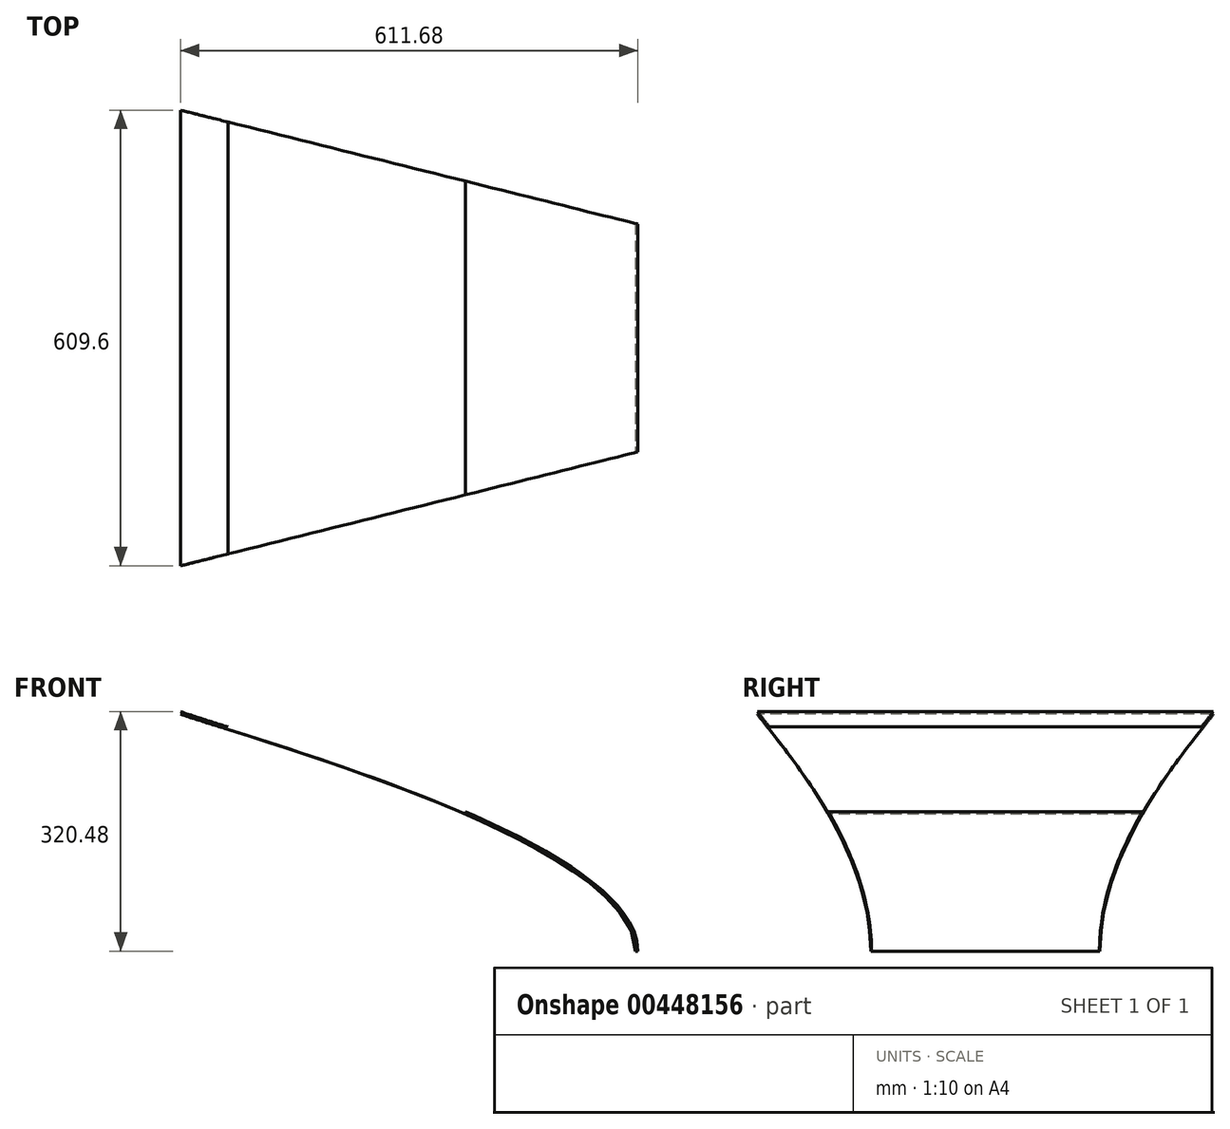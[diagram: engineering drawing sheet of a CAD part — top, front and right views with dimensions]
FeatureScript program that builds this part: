
annotation { "Feature Type Name" : "Feature", "Feature Type Description" : "" }
export const myFeature = defineFeature(function(context is Context, id is Id, definition is map)
    precondition{}
    {
        {
            var Q0;
            Q0=qCreatedBy(makeId("Front.planeOp"),FACE);
            var sketch = newSketch(context, id + "F0", { "sketchPlane" : qUnion([Q0])});
            skFitSpline(sketch, "E0", {"points": [v(-609.6, 317.5) * mm, v(0, 0) * mm], "startDerivative": vector(239.16, -88.23) * mm, "endDerivative": vector(0, -441.17) * mm});
            skSolve(sketch);
        }
        {
            var Q0;
            Q0=qCreatedBy(makeId("Top.planeOp"),FACE);
            var sketch = newSketch(context, id + "F1", { "sketchPlane" : qUnion([Q0])});
            skLineSegment(sketch, "E1.bottom", {"start": v(0, 304.8) * mm, "end": v(3.18, 304.8) * mm});
            skLineSegment(sketch, "E1.top", {"start": v(0, -304.8) * mm, "end": v(3.18, -304.8) * mm});
            skLineSegment(sketch, "E1.left", {"start": v(0, 304.8) * mm, "end": v(0, -304.8) * mm});
            skLineSegment(sketch, "E1.right", {"start": v(3.17, 304.8) * mm, "end": v(3.18, -304.8) * mm});
            skSolve(sketch);
        }
        {
            var Q0;
            Q0=makeQuery(id+"F1.imprint","IMPRINT",FACE,{"disambiguationData":[TD([[makeQuery(id+"F1.imprint","IMPRINT",EDGE,{"derivedFrom":sQuery(id+"F1.wireOp",EDGE,"E1.bottom")}),-1.0]])]});
            var Q1;
            Q1=sQuery(id+"F0.wireOp",EDGE,"E0");
            sweep(context, id + "F2", {"profiles" : qUnion([Q0]), "path" : qUnion([Q1])});
        }
        {
            var Q0;
            Q0=qCreatedBy(makeId("Top.planeOp"),FACE);
            var sketch = newSketch(context, id + "F3", { "sketchPlane" : qUnion([Q0])});
            skFitSpline(sketch, "E2.0.0", {"points": [v(3.17, 304.8) * mm, v(-200.72, 304.8) * mm, v(-404.6, 304.8) * mm, v(-608.5, 304.8) * mm]});
            skLineSegment(sketch, "E2.0.1", {"start": v(-608.5, -304.8) * mm, "end": v(-608.5, 304.8) * mm});
            skFitSpline(sketch, "E2.0.2", {"points": [v(-608.5, -304.8) * mm, v(-404.6, -304.8) * mm, v(-200.72, -304.8) * mm, v(3.18, -304.8) * mm]});
            skLineSegment(sketch, "E2.0.3", {"start": v(3.18, -304.8) * mm, "end": v(3.17, 304.8) * mm});
            skLineSegment(sketch, "E3", {"start": v(-608.5, 304.8) * mm, "end": v(3.18, 152.4) * mm});
            skLineSegment(sketch, "E4", {"start": v(-608.5, -304.8) * mm, "end": v(3.18, -152.4) * mm});
            skLineSegment(sketch, "E5", {"start": v(-608.5, 304.8) * mm, "end": v(3.17, 304.8) * mm});
            skLineSegment(sketch, "E6", {"start": v(3.18, 152.4) * mm, "end": v(3.17, 304.8) * mm});
            skLineSegment(sketch, "E7", {"start": v(-608.5, -304.8) * mm, "end": v(3.18, -304.8) * mm});
            skLineSegment(sketch, "E8", {"start": v(3.18, -152.4) * mm, "end": v(3.18, -304.8) * mm});
            skSolve(sketch);
        }
        {
            var Q0;
            Q0=makeQuery(id+"F3.imprint","IMPRINT",FACE,{"disambiguationData":[TD([[makeQuery(id+"F3.imprint","IMPRINT",EDGE,{"derivedFrom":sQuery(id+"F3.wireOp",EDGE,"E4")}),-1.0]])]});
            var Q1;
            Q1=makeQuery(id+"F3.imprint","IMPRINT",FACE,{"disambiguationData":[TD([[makeQuery(id+"F3.imprint","IMPRINT",EDGE,{"derivedFrom":sQuery(id+"F3.wireOp",EDGE,"E3")}),1.0]])]});
            extrude(context, id + "F4", {"entities" : qUnion([Q0, Q1]), "operationType" : NewBodyOperationType.REMOVE, "endBound" : BoundingType.THROUGH_ALL, "depth" : 25.4 * mm});
        }
        {
            var Q0;
            Q0=qCreatedBy(makeId("Front.planeOp"),FACE);
            cPlane(context, id + "F5", {"entities" : qUnion([Q0]), "cplaneType" : CPlaneType.OFFSET, "offset" : 609.6 * mm, "width" : 152.4 * mm, "height" : 152.4 * mm});
        }
        {
            var Q0;
            Q0=qCreatedBy(id+"F5.planeOp",FACE);
            var sketch = newSketch(context, id + "F6", { "sketchPlane" : qUnion([Q0])});
            skFitSpline(sketch, "E9.0.0", {"points": [v(-608.5, 317.1) * mm, v(-606.77, 316.47) * mm, v(-603.3, 315.25) * mm, v(-596.35, 312.9) * mm, v(-587.63, 310.05) * mm, v(-577.14, 306.7) * mm, v(-566.64, 303.37) * mm, v(-556.14, 300.07) * mm, v(-542.13, 295.67) * mm, v(-524.62, 290.17) * mm, v(-503.62, 283.52) * mm, v(-482.65, 276.8) * mm, v(-461.7, 270) * mm, v(-433.8, 260.8) * mm, v(-399.03, 249.03) * mm, v(-357.45, 234.37) * mm, v(-316.1, 219.1) * mm, v(-275.05, 203.1) * mm, v(-241.12, 189.02) * mm, v(-214.18, 177.21) * mm, v(-197.45, 169.58) * mm, v(-184.13, 163.29) * mm, v(-170.85, 156.88) * mm, v(-154.38, 148.62) * mm, v(-138.09, 140) * mm, v(-125.2, 132.83) * mm, v(-115.6, 127.32) * mm, v(-106.08, 121.64) * mm, v(-93.5, 113.85) * mm, v(-78.12, 103.67) * mm, v(-63.24, 92.76) * mm, v(-51.75, 83.45) * mm, v(-44.77, 77.36) * mm, v(-39.32, 72.28) * mm, v(-35.31, 68.37) * mm, v(-31.41, 64.35) * mm, v(-27.63, 60.23) * mm, v(-23.98, 55.99) * mm, v(-20.47, 51.62) * mm, v(-17.68, 47.86) * mm, v(-15.54, 44.78) * mm, v(-13.46, 41.63) * mm, v(-11, 37.62) * mm, v(-8.34, 32.68) * mm, v(-6.35, 28.44) * mm, v(-4.93, 24.97) * mm, v(-3.95, 22.32) * mm, v(-3.2, 20.08) * mm, v(-2.66, 18.26) * mm, v(-2.15, 16.42) * mm, v(-1.58, 14.11) * mm, v(-0.82, 10.4) * mm, v(-0.18, 5.71) * mm, v(0, 1.91) * mm, v(0, 0) * mm]});
            skLineSegment(sketch, "E9.0.1", {"start": v(0, 0) * mm, "end": v(3.18, 0) * mm});
            skFitSpline(sketch, "E9.0.2", {"points": [v(3.17, 0) * mm, v(3.17, 1.95) * mm, v(3, 5.81) * mm, v(2.24, 11.52) * mm, v(1.01, 17.13) * mm, v(-0.37, 21.73) * mm, v(-1.68, 25.38) * mm, v(-2.75, 28.06) * mm, v(-3.9, 30.7) * mm, v(-5.54, 34.15) * mm, v(-7.77, 38.35) * mm, v(-10.7, 43.24) * mm, v(-13.33, 47.2) * mm, v(-15.55, 50.3) * mm, v(-17.26, 52.6) * mm, v(-19.01, 54.87) * mm, v(-21.4, 57.83) * mm, v(-24.47, 61.44) * mm, v(-28.26, 65.64) * mm, v(-33.47, 71.06) * mm, v(-40.2, 77.56) * mm, v(-48.62, 84.97) * mm, v(-57.3, 92.07) * mm, v(-66.23, 98.88) * mm, v(-73.84, 104.36) * mm, v(-80.02, 108.63) * mm, v(-86.23, 112.82) * mm, v(-94.06, 117.91) * mm, v(-103.54, 123.82) * mm, v(-116.3, 131.45) * mm, v(-132.43, 140.58) * mm, v(-152.02, 150.99) * mm, v(-171.82, 160.93) * mm, v(-198.46, 173.67) * mm, v(-232.14, 188.72) * mm, v(-273.03, 205.7) * mm, v(-307.44, 219.13) * mm, v(-335.12, 229.5) * mm, v(-362.9, 239.66) * mm, v(-397.76, 251.95) * mm, v(-432.75, 263.8) * mm, v(-460.81, 273.05) * mm, v(-481.89, 279.9) * mm, v(-503, 286.65) * mm, v(-524.12, 293.34) * mm, v(-541.74, 298.87) * mm, v(-555.83, 303.3) * mm, v(-566.4, 306.62) * mm, v(-576.96, 309.97) * mm, v(-587.51, 313.35) * mm, v(-596.29, 316.22) * mm, v(-603.28, 318.6) * mm, v(-606.77, 319.84) * mm, v(-608.5, 320.48) * mm]});
            skLineSegment(sketch, "E10.bottom", {"start": v(-608.5, 320.48) * mm, "end": v(-227.5, 320.48) * mm});
            skLineSegment(sketch, "E10.top", {"start": v(-608.5, 30.09) * mm, "end": v(-227.5, 30.09) * mm});
            skLineSegment(sketch, "E10.left", {"start": v(-608.5, 317.1) * mm, "end": v(-608.5, 30.09) * mm});
            skLineSegment(sketch, "E10.right", {"start": v(-227.5, 320.48) * mm, "end": v(-227.5, 30.09) * mm});
            skLineSegment(sketch, "E11", {"start": v(-608.5, 320.48) * mm, "end": v(-599.5, 336.89) * mm});
            skLineSegment(sketch, "E12", {"start": v(-599.5, 336.89) * mm, "end": v(-625.28, 339.03) * mm});
            skLineSegment(sketch, "E13", {"start": v(-625.28, 339.03) * mm, "end": v(-641.72, 325.34) * mm});
            skLineSegment(sketch, "E14", {"start": v(-641.72, 325.34) * mm, "end": v(-633.04, 302.49) * mm});
            skLineSegment(sketch, "E15", {"start": v(-633.04, 302.49) * mm, "end": v(-616.69, 302.49) * mm});
            skLineSegment(sketch, "E16", {"start": v(-616.69, 302.49) * mm, "end": v(-608.5, 317.1) * mm});
            skSolve(sketch);
        }
        {
            var Q0;
            {var subQ0=sQuery(id+"F6.wireOp",EDGE,"E10.left");var subQ1=sQuery(id+"F6.wireOp",EDGE,"E9.0.0");var subQ2=makeQuery(id+"F6.imprint","INTERSECT",VERTEX,{"derivedFrom":[subQ1,subQ0]});Q0=makeQuery(id+"F6.imprint","IMPRINT",FACE,{"disambiguationData":[TD([[makeQuery(id+"F6.imprint","IMPRINT",EDGE,{"disambiguationData":[TD([[subQ2,-1.0]])],"derivedFrom":subQ1}),1.0]])]});}
            extrude(context, id + "F7", {"entities" : qUnion([Q0]), "operationType" : NewBodyOperationType.REMOVE, "endBound" : BoundingType.THROUGH_ALL, "oppositeDirection" : true, "depth" : 25.4 * mm});
        }
    });
